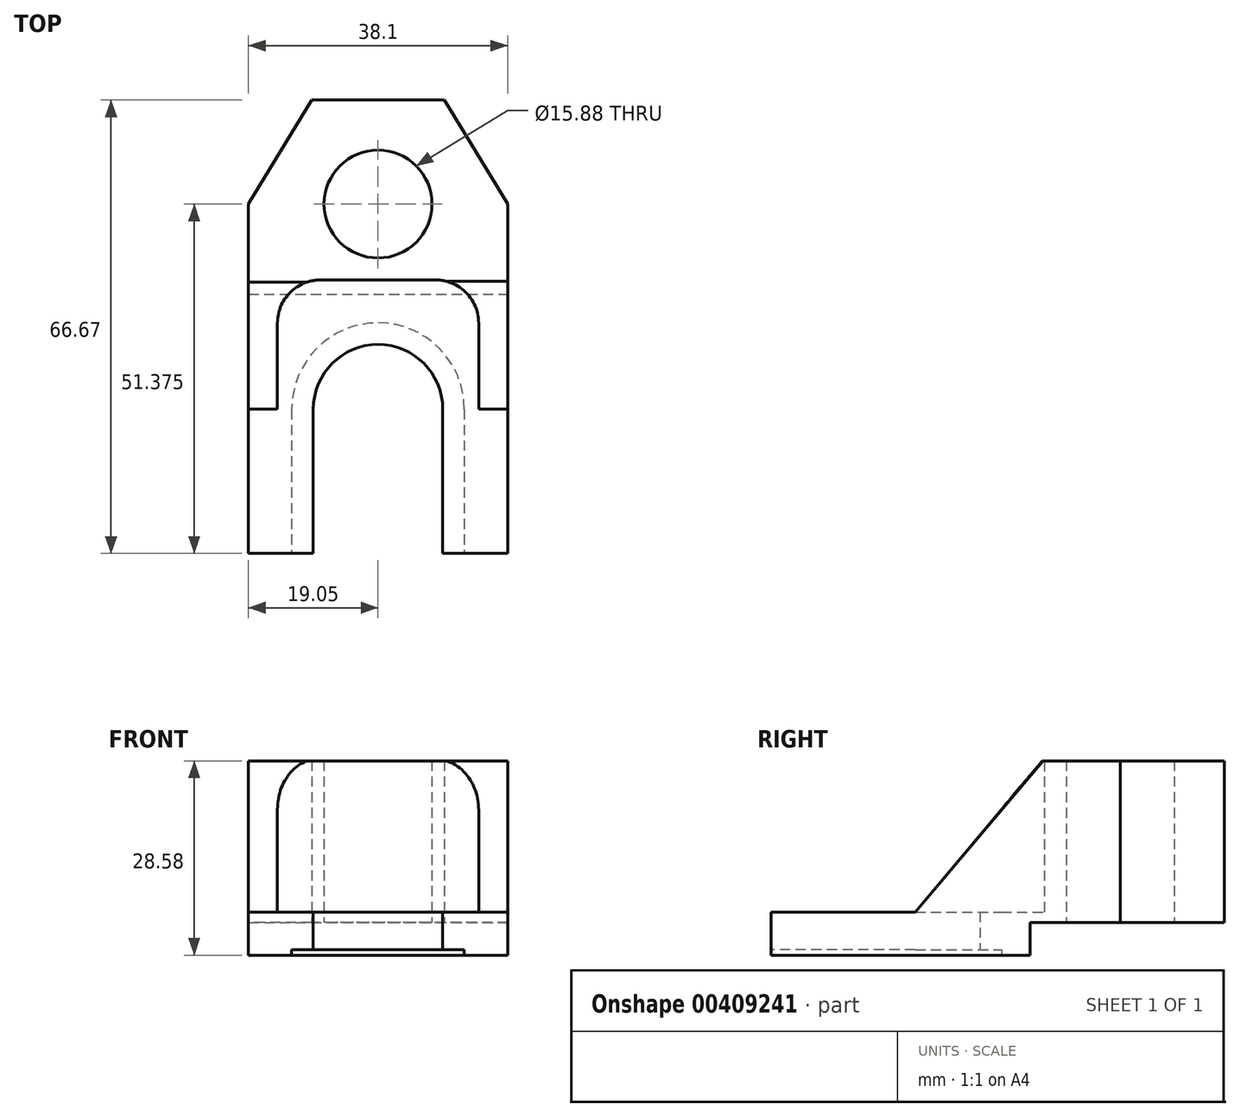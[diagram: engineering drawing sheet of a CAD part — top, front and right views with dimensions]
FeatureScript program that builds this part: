
annotation { "Feature Type Name" : "Feature", "Feature Type Description" : "" }
export const myFeature = defineFeature(function(context is Context, id is Id, definition is map)
    precondition{}
    {
        {
            var Q0;
            Q0=qCreatedBy(makeId("Top.planeOp"),FACE);
            var sketch = newSketch(context, id + "F0", { "sketchPlane" : qUnion([Q0])});
            skArc(sketch, "E0", {"start": v(9.53, 0) * mm, "mid": v(0, 9.53) * mm, "end": v(-9.53, 0) * mm});
            skCircle(sketch, "E1", {"center": v(0, 30.18) * mm, "radius": 7.94 * mm});
            skLineSegment(sketch, "E2", {"start": v(-19.05, -21.2) * mm, "end": v(-9.53, -21.2) * mm});
            skLineSegment(sketch, "E3", {"start": v(19.05, -21.2) * mm, "end": v(19.05, 30.18) * mm});
            skLineSegment(sketch, "E4", {"start": v(19.05, 30.18) * mm, "end": v(9.77, 45.47) * mm});
            skLineSegment(sketch, "E5", {"start": v(9.77, 45.47) * mm, "end": v(-9.77, 45.47) * mm});
            skLineSegment(sketch, "E6", {"start": v(-9.77, 45.47) * mm, "end": v(-19.05, 30.18) * mm});
            skLineSegment(sketch, "E7", {"start": v(-19.05, 30.18) * mm, "end": v(-19.05, -21.2) * mm});
            skLineSegment(sketch, "E8", {"start": v(-9.53, 0) * mm, "end": v(-9.53, -21.2) * mm});
            skLineSegment(sketch, "E9", {"start": v(9.53, 0) * mm, "end": v(9.53, -21.2) * mm});
            skLineSegment(sketch, "E10.trimOffspring", {"start": v(9.53, -21.2) * mm, "end": v(19.05, -21.2) * mm});
            skPoint(sketch, "E11.end.orphan", {"position": v(-12.7, 0) * mm});
            skPoint(sketch, "E12.start.orphan", {"position": v(12.7, 0) * mm});
            skSolve(sketch);
        }
        {
            var Q0;
            Q0 = qSketchRegion(id + "F0", true);
            extrude(context, id + "F1", {"entities" : qUnion([Q0]), "depth" : 28.57 * mm});
        }
        {
            var Q0;
            Q0=makeQuery(id+"F1.opExtrude","CAP_FACE",FACE,{"disambiguationData":[OSD([sQuery(id+"F0.wireOp",EDGE,"E0"),sQuery(id+"F0.wireOp",EDGE,"E1"),sQuery(id+"F0.wireOp",EDGE,"E2"),sQuery(id+"F0.wireOp",EDGE,"E3"),sQuery(id+"F0.wireOp",EDGE,"E4"),sQuery(id+"F0.wireOp",EDGE,"E5"),sQuery(id+"F0.wireOp",EDGE,"E6"),sQuery(id+"F0.wireOp",EDGE,"E7"),sQuery(id+"F0.wireOp",EDGE,"E8"),sQuery(id+"F0.wireOp",EDGE,"E9"),sQuery(id+"F0.wireOp",EDGE,"E10.trimOffspring")])],"isStart":true});
            var sketch = newSketch(context, id + "F2", { "sketchPlane" : qUnion([Q0])});
            skArc(sketch, "E13", {"start": v(-12.7, 0) * mm, "mid": v(0, -12.7) * mm, "end": v(12.7, 0) * mm});
            skLineSegment(sketch, "E14", {"start": v(-12.7, 0) * mm, "end": v(-12.7, 21.2) * mm});
            skLineSegment(sketch, "E15", {"start": v(12.7, 0) * mm, "end": v(12.7, 21.2) * mm});
            skLineSegment(sketch, "E16", {"start": v(-19.05, -16.9) * mm, "end": v(19.05, -16.9) * mm});
            skSolve(sketch);
        }
        {
            var Q0;
            Q0=makeQuery(id+"F2.imprint","IMPRINT",FACE,{"disambiguationData":[TD([[makeQuery(id+"F2.imprint","IMPRINT",EDGE,{"derivedFrom":sQuery(id+"F2.wireOp",EDGE,"E13")}),1.0]])]});
            extrude(context, id + "F3", {"entities" : qUnion([Q0]), "operationType" : NewBodyOperationType.REMOVE, "oppositeDirection" : true, "depth" : 0.81 * mm});
        }
        {
            var Q0;
            {var subQ3=sQuery(id+"F2.wireOp",EDGE,"E16");Q0=makeQuery(id+"F2.imprint","IMPRINT",FACE,{"disambiguationData":[TD([[makeQuery(id+"F2.imprint","IMPRINT",EDGE,{"derivedFrom":subQ3}),-1.0]])]});}
            extrude(context, id + "F4", {"entities" : qUnion([Q0]), "operationType" : NewBodyOperationType.REMOVE, "oppositeDirection" : true, "depth" : 4.78 * mm});
        }
        {
            var Q0;
            Q0=makeQuery(id+"F1.opExtrude","CAP_FACE",FACE,{"disambiguationData":[OSD([sQuery(id+"F0.wireOp",EDGE,"E0"),sQuery(id+"F0.wireOp",EDGE,"E1"),sQuery(id+"F0.wireOp",EDGE,"E2"),sQuery(id+"F0.wireOp",EDGE,"E3"),sQuery(id+"F0.wireOp",EDGE,"E4"),sQuery(id+"F0.wireOp",EDGE,"E5"),sQuery(id+"F0.wireOp",EDGE,"E6"),sQuery(id+"F0.wireOp",EDGE,"E7"),sQuery(id+"F0.wireOp",EDGE,"E8"),sQuery(id+"F0.wireOp",EDGE,"E9"),sQuery(id+"F0.wireOp",EDGE,"E10.trimOffspring")])],"isStart":false});
            var sketch = newSketch(context, id + "F5", { "sketchPlane" : qUnion([Q0])});
            skPoint(sketch, "E17.end.orphan", {"position": v(14.8, 0) * mm});
            skPoint(sketch, "E18.start.orphan", {"position": v(-14.8, 0) * mm});
            skLineSegment(sketch, "E19", {"start": v(-14.8, 0) * mm, "end": v(-14.8, 19.02) * mm});
            skLineSegment(sketch, "E20", {"start": v(-14.8, 19.02) * mm, "end": v(14.8, 19.02) * mm});
            skLineSegment(sketch, "E21", {"start": v(14.8, 19.02) * mm, "end": v(14.8, 0) * mm});
            skLineSegment(sketch, "E22", {"start": v(-14.8, 0) * mm, "end": v(-19.05, 0) * mm});
            skLineSegment(sketch, "E23", {"start": v(14.8, 0) * mm, "end": v(19.05, 0) * mm});
            skSolve(sketch);
        }
        {
            var Q0;
            Q0=makeQuery(id+"F5.imprint","IMPRINT",FACE,{"disambiguationData":[TD([[makeQuery(id+"F5.imprint","IMPRINT",EDGE,{"derivedFrom":sQuery(id+"F5.wireOp",EDGE,"E19")}),-1.0]])]});
            extrude(context, id + "F6", {"entities" : qUnion([Q0]), "operationType" : NewBodyOperationType.REMOVE, "oppositeDirection" : true, "depth" : 22.22 * mm});
        }
        {
            var Q0;
            Q0=makeQuery(id+"F1.opExtrude","SWEPT_FACE",FACE,{"disambiguationData":[OSD([sQuery(id+"F0.wireOp",EDGE,"E3")])]});
            var sketch = newSketch(context, id + "F7", { "sketchPlane" : qUnion([Q0])});
            skLineSegment(sketch, "E24", {"start": v(0, 6.35) * mm, "end": v(18.82, 28.58) * mm});
            skSolve(sketch);
        }
        {
            var Q0;
            {var subQ0=sQuery(id+"F7.wireOp",EDGE,"E24");Q0=makeQuery(id+"F7.imprint","IMPRINT",FACE,{"disambiguationData":[TD([[makeQuery(id+"F7.imprint","IMPRINT",EDGE,{"derivedFrom":subQ0}),1.0]])]});}
            extrude(context, id + "F8", {"entities" : qUnion([Q0]), "operationType" : NewBodyOperationType.REMOVE, "oppositeDirection" : true, "depth" : 25.4 * mm});
        }
        {
            var Q0;
            Q0=makeQuery(id+"F1.opExtrude","SWEPT_FACE",FACE,{"disambiguationData":[OSD([sQuery(id+"F0.wireOp",EDGE,"E7")])]});
            var sketch = newSketch(context, id + "F9", { "sketchPlane" : qUnion([Q0])});
            skLineSegment(sketch, "E25", {"start": v(0, 6.35) * mm, "end": v(-18.67, 28.58) * mm});
            skSolve(sketch);
        }
        {
            var Q0;
            {var subQ0=sQuery(id+"F9.wireOp",EDGE,"E25");Q0=makeQuery(id+"F9.imprint","IMPRINT",FACE,{"disambiguationData":[TD([[makeQuery(id+"F9.imprint","IMPRINT",EDGE,{"derivedFrom":subQ0}),-1.0]])]});}
            extrude(context, id + "F10", {"entities" : qUnion([Q0]), "operationType" : NewBodyOperationType.REMOVE, "oppositeDirection" : true, "depth" : 25.4 * mm});
        }
        {
            var Q0;
            Q0=makeQuery(id+"F6.boolean.opBoolean","COPY",EDGE,{"derivedFrom":makeQuery(id+"F6.opExtrude","SWEPT_EDGE",EDGE,{"disambiguationData":[OSD([sQuery(id+"F5.wireOp",EDGE,"E19"),sQuery(id+"F5.wireOp",EDGE,"E20")])]})});
            var Q1;
            Q1=makeQuery(id+"F6.boolean.opBoolean","COPY",EDGE,{"derivedFrom":makeQuery(id+"F6.opExtrude","SWEPT_EDGE",EDGE,{"disambiguationData":[OSD([sQuery(id+"F5.wireOp",EDGE,"E20"),sQuery(id+"F5.wireOp",EDGE,"E21")])]})});
            fillet(context, id + "F11", {"entities" : qUnion([Q0, Q1]), "radius" : 6.35 * mm, "tangentPropagation" : true, "allowEdgeOverflow" : false});
        }
    });
